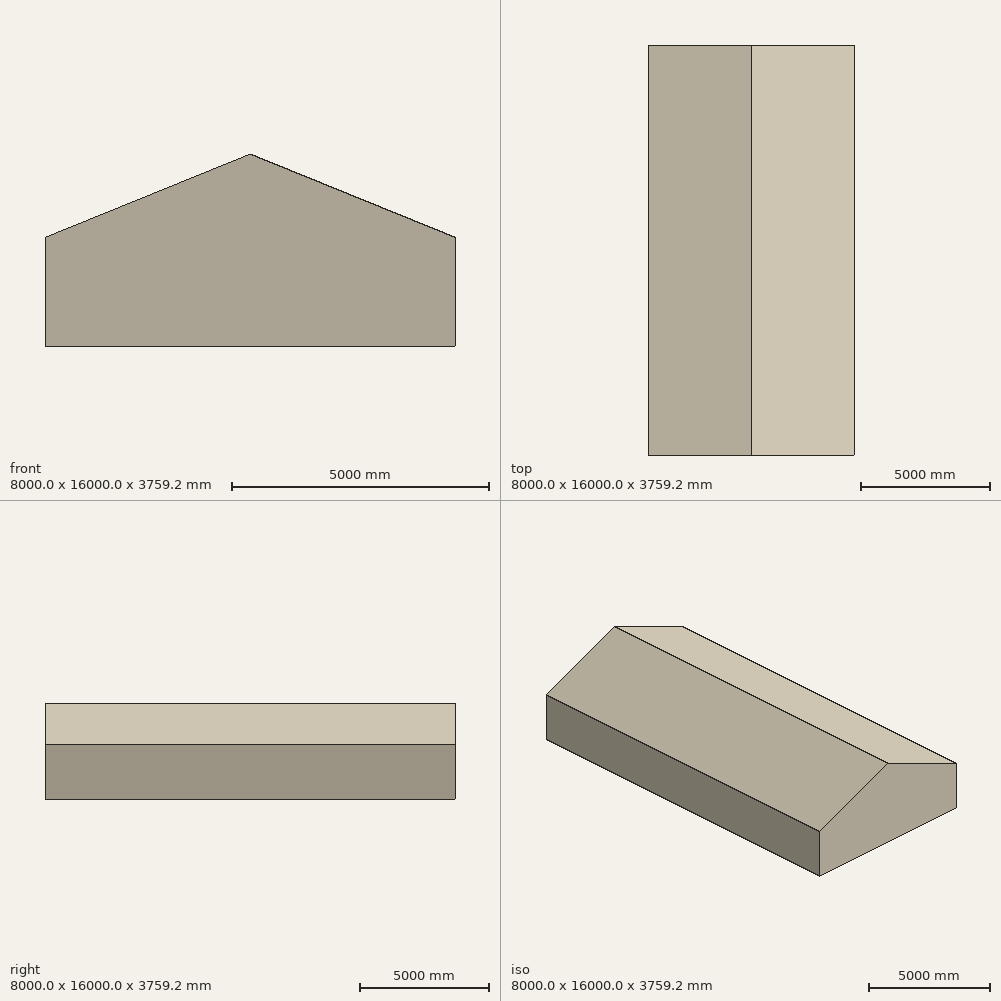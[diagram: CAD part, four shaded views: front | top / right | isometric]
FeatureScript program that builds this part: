
annotation { "Feature Type Name" : "Feature", "Feature Type Description" : "" }
export const myFeature = defineFeature(function(context is Context, id is Id, definition is map)
    precondition{}
    {
        {
            var Q0;
            Q0=qCreatedBy(makeId("Top.planeOp"),FACE);
            var sketch = newSketch(context, id + "F0", { "sketchPlane" : qUnion([Q0])});
            skLineSegment(sketch, "E0.bottom", {"start": v(0, 0) * mm, "end": v(-8000, 0) * mm});
            skLineSegment(sketch, "E0.top", {"start": v(0, 16000) * mm, "end": v(-8000, 16000) * mm});
            skLineSegment(sketch, "E0.left", {"start": v(0, 0) * mm, "end": v(0, 16000) * mm});
            skLineSegment(sketch, "E0.right", {"start": v(-8000, 0) * mm, "end": v(-8000, 16000) * mm});
            skSolve(sketch);
        }
        {
            var Q0;
            Q0=makeQuery(id+"F0.imprint","IMPRINT",FACE,{"disambiguationData":[TD([[makeQuery(id+"F0.imprint","IMPRINT",EDGE,{"derivedFrom":sQuery(id+"F0.wireOp",EDGE,"E0.bottom")}),-1.0]])]});
            extrude(context, id + "F1", {"entities" : qUnion([Q0]), "depth" : 3759.2 * mm, "offsetDistance" : 25 * mm});
        }
        {
            var Q0;
            Q0=makeQuery(id+"F1.opExtrude","SWEPT_FACE",FACE,{"disambiguationData":[OSD([sQuery(id+"F0.wireOp",EDGE,"E0.bottom")])]});
            var sketch = newSketch(context, id + "F2", { "sketchPlane" : qUnion([Q0])});
            skLineSegment(sketch, "E1", {"start": v(0, 0) * mm, "end": v(0, 2133.6) * mm});
            skLineSegment(sketch, "E2", {"start": v(0, 2133.6) * mm, "end": v(-4000, 3759.2) * mm});
            skLineSegment(sketch, "E3", {"start": v(-4000, 3759.2) * mm, "end": v(-8000, 2133.6) * mm});
            skLineSegment(sketch, "E4", {"start": v(-8000, 2133.6) * mm, "end": v(-8000, 0) * mm});
            skSolve(sketch);
        }
        {
            var Q0;
            {var subQ0=sQuery(id+"F2.wireOp",EDGE,"E2");Q0=makeQuery(id+"F2.imprint","IMPRINT",FACE,{"disambiguationData":[TD([[makeQuery(id+"F2.imprint","IMPRINT",EDGE,{"derivedFrom":subQ0}),-1.0]])]});}
            var Q1;
            {var subQ0=sQuery(id+"F2.wireOp",EDGE,"E3");Q1=makeQuery(id+"F2.imprint","IMPRINT",FACE,{"disambiguationData":[TD([[makeQuery(id+"F2.imprint","IMPRINT",EDGE,{"derivedFrom":subQ0}),-1.0]])]});}
            extrude(context, id + "F3", {"entities" : qUnion([Q0, Q1]), "operationType" : NewBodyOperationType.REMOVE, "oppositeDirection" : true, "depth" : 16000 * mm, "offsetDistance" : 25 * mm});
        }
        {
            var Q0;
            Q0=makeQuery(id+"F1.opExtrude","CAP_FACE",FACE,{"disambiguationData":[OSD([sQuery(id+"F0.wireOp",EDGE,"E0.bottom"),sQuery(id+"F0.wireOp",EDGE,"E0.top"),sQuery(id+"F0.wireOp",EDGE,"E0.left"),sQuery(id+"F0.wireOp",EDGE,"E0.right")])],"isStart":true});
            var sketch = newSketch(context, id + "F4", { "sketchPlane" : qUnion([Q0])});
            skLineSegment(sketch, "E5", {"start": v(-8000, 0) * mm, "end": v(0, -16000) * mm});
            skLineSegment(sketch, "E6.bottom", {"start": v(-85.6, -15828.82) * mm, "end": v(-7914.4, -15828.82) * mm});
            skLineSegment(sketch, "E6.top", {"start": v(-85.6, -171.18) * mm, "end": v(-7914.4, -171.18) * mm});
            skLineSegment(sketch, "E6.left", {"start": v(-85.6, -15828.82) * mm, "end": v(-85.6, -171.18) * mm});
            skLineSegment(sketch, "E6.right", {"start": v(-7914.4, -15828.82) * mm, "end": v(-7914.4, -171.18) * mm});
            skPoint(sketch, "E6.middle", {"position": v(-4000, -8000) * mm});
            skSolve(sketch);
        }
        {
            var Q0;
            {var subQ0=sQuery(id+"F4.wireOp",EDGE,"E6.bottom");Q0=makeQuery(id+"F4.imprint","IMPRINT",FACE,{"disambiguationData":[TD([[makeQuery(id+"F4.imprint","IMPRINT",EDGE,{"derivedFrom":subQ0}),-1.0]])]});}
            var Q1;
            {var subQ2=sQuery(id+"F4.wireOp",EDGE,"E6.top");Q1=makeQuery(id+"F4.imprint","IMPRINT",FACE,{"disambiguationData":[TD([[makeQuery(id+"F4.imprint","IMPRINT",EDGE,{"derivedFrom":subQ2}),1.0]])]});}
            extrude(context, id + "F5", {"entities" : qUnion([Q0, Q1]), "operationType" : NewBodyOperationType.REMOVE, "oppositeDirection" : true, "depth" : 2133.6 * mm, "offsetDistance" : 25 * mm});
        }
        {
            var Q0;
            Q0=makeQuery(id+"F1.opExtrude","SWEPT_FACE",FACE,{"disambiguationData":[OSD([sQuery(id+"F0.wireOp",EDGE,"E0.bottom")])]});
            var sketch = newSketch(context, id + "F6", { "sketchPlane" : qUnion([Q0])});
            skLineSegment(sketch, "E7", {"start": v(-8000, 2133.6) * mm, "end": v(-7850, 2133.6) * mm});
            skLineSegment(sketch, "E8", {"start": v(-7850, 2133.6) * mm, "end": v(-4428.09, 3524.26) * mm});
            skLineSegment(sketch, "E9", {"start": v(0, 2133.6) * mm, "end": v(-150, 2133.6) * mm});
            skLineSegment(sketch, "E10", {"start": v(-7850, 2133.6) * mm, "end": v(-150, 2133.6) * mm});
            skLineSegment(sketch, "E11", {"start": v(-4000, 3759.2) * mm, "end": v(-4000, 3458.3) * mm});
            skLineSegment(sketch, "E12", {"start": v(-4428.09, 3524.26) * mm, "end": v(-4000, 3698.24) * mm});
            skPoint(sketch, "E12.endSnap0", {"position": v(-4000, 3608.75) * mm});
            skLineSegment(sketch, "E13", {"start": v(-150, 2133.6) * mm, "end": v(-4000, 3698.24) * mm});
            skSolve(sketch);
        }
        {
            var Q0;
            Q0=makeQuery(id+"F6.imprint","IMPRINT",FACE,{"disambiguationData":[TD([[makeQuery(id+"F6.imprint","IMPRINT",EDGE,{"derivedFrom":sQuery(id+"F6.wireOp",EDGE,"E8")}),-1.0]])]});
            extrude(context, id + "F7", {"entities" : qUnion([Q0]), "operationType" : NewBodyOperationType.REMOVE, "oppositeDirection" : true, "depth" : 15900 * mm, "offsetDistance" : 25 * mm});
        }
        {
            var Q0;
            Q0=makeQuery(id+"F1.opExtrude","SWEPT_FACE",FACE,{"disambiguationData":[OSD([sQuery(id+"F0.wireOp",EDGE,"E0.bottom")])]});
            var sketch = newSketch(context, id + "F8", { "sketchPlane" : qUnion([Q0])});
            skLineSegment(sketch, "E14", {"start": v(-7850, 2133.6) * mm, "end": v(-150, 2133.6) * mm});
            skLineSegment(sketch, "E15", {"start": v(-150, 2133.6) * mm, "end": v(-7850, 2133.6) * mm});
            skLineSegment(sketch, "E16", {"start": v(-7850, 2133.6) * mm, "end": v(-7850, 2133.6) * mm});
            skLineSegment(sketch, "E17", {"start": v(-4000, 3698.24) * mm, "end": v(-7850, 2133.6) * mm});
            skSolve(sketch);
        }
        {
            var Q0;
            Q0=makeQuery(id+"F8.imprint","IMPRINT",FACE,{"disambiguationData":[TD([[makeQuery(id+"F8.imprint","IMPRINT",EDGE,{"derivedFrom":sQuery(id+"F8.wireOp",EDGE,"E14")}),1.0]])]});
            extrude(context, id + "F9", {"entities" : qUnion([Q0]), "operationType" : NewBodyOperationType.ADD, "oppositeDirection" : true, "depth" : 100 * mm, "offsetDistance" : 25 * mm});
        }
    });
